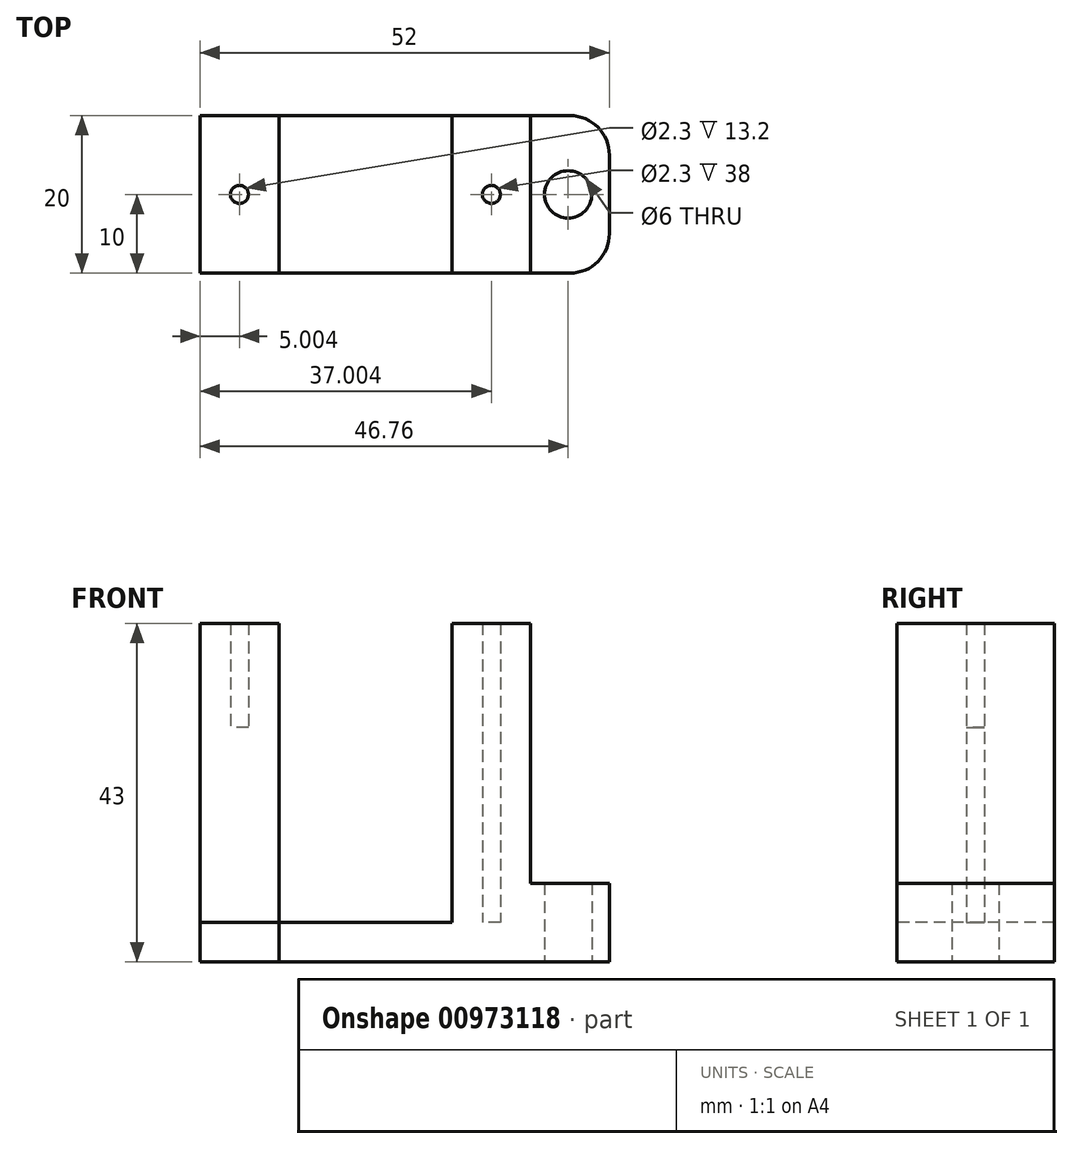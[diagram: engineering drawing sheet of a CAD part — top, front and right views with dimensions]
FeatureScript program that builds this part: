
annotation { "Feature Type Name" : "Feature", "Feature Type Description" : "" }
export const myFeature = defineFeature(function(context is Context, id is Id, definition is map)
    precondition{}
    {
        {
            var Q0;
            Q0=qCreatedBy(makeId("Top.planeOp"),FACE);
            var sketch = newSketch(context, id + "F0", { "sketchPlane" : qUnion([Q0])});
            skLineSegment(sketch, "E0.bottom", {"start": v(-30.4, 24.22) * mm, "end": v(11.6, 24.22) * mm});
            skLineSegment(sketch, "E0.top", {"start": v(-30.4, 4.22) * mm, "end": v(11.6, 4.22) * mm});
            skLineSegment(sketch, "E0.left", {"start": v(-30.4, 24.22) * mm, "end": v(-30.4, 4.22) * mm});
            skLineSegment(sketch, "E0.right", {"start": v(11.6, 24.22) * mm, "end": v(11.6, 4.22) * mm});
            skLineSegment(sketch, "E1", {"start": v(-20.4, 24.22) * mm, "end": v(-20.4, 4.22) * mm});
            skLineSegment(sketch, "E2", {"start": v(1.6, 24.22) * mm, "end": v(1.6, 4.22) * mm});
            skCircle(sketch, "E3", {"center": v(-25.4, 14.22) * mm, "radius": 1.15 * mm});
            skCircle(sketch, "E4", {"center": v(6.6, 14.22) * mm, "radius": 1.15 * mm});
            skLineSegment(sketch, "E5.bottom", {"start": v(11.6, 24.22) * mm, "end": v(21.6, 24.22) * mm});
            skLineSegment(sketch, "E5.top", {"start": v(11.6, 4.22) * mm, "end": v(21.6, 4.22) * mm});
            skLineSegment(sketch, "E5.right", {"start": v(21.6, 24.22) * mm, "end": v(21.6, 4.22) * mm});
            skCircle(sketch, "E6", {"center": v(16.36, 14.22) * mm, "radius": 3 * mm});
            skSolve(sketch);
        }
        {
            var Q0;
            {var subQ0=sQuery(id+"F0.wireOp",EDGE,"E0.left");Q0=makeQuery(id+"F0.imprint","IMPRINT",FACE,{"disambiguationData":[TD([[makeQuery(id+"F0.imprint","IMPRINT",EDGE,{"derivedFrom":subQ0}),1.0]])]});}
            var Q1;
            {var subQ1=sQuery(id+"F0.wireOp",EDGE,"E0.right");Q1=makeQuery(id+"F0.imprint","IMPRINT",FACE,{"disambiguationData":[TD([[makeQuery(id+"F0.imprint","IMPRINT",EDGE,{"derivedFrom":subQ1}),-1.0]])]});}
            var Q2;
            Q2=makeQuery(id+"F0.imprint","IMPRINT",FACE,{"disambiguationData":[TD([[makeQuery(id+"F0.imprint","IMPRINT",EDGE,{"derivedFrom":sQuery(id+"F0.wireOp",EDGE,"E3")}),1.0]])]});
            var Q3;
            {var subQ0=sQuery(id+"F0.wireOp",EDGE,"E2");Q3=makeQuery(id+"F0.imprint","IMPRINT",FACE,{"disambiguationData":[TD([[makeQuery(id+"F0.imprint","IMPRINT",EDGE,{"derivedFrom":subQ0}),1.0]])]});}
            extrude(context, id + "F1", {"entities" : qUnion([Q0, Q1, Q2, Q3]), "depth" : 43 * mm, "offsetDistance" : 25 * mm});
        }
        {
            var Q0;
            {var subQ0=sQuery(id+"F0.wireOp",EDGE,"E0.left");Q0=makeQuery(id+"F0.imprint","IMPRINT",FACE,{"disambiguationData":[TD([[makeQuery(id+"F0.imprint","IMPRINT",EDGE,{"derivedFrom":subQ0}),1.0]])]});}
            var Q1;
            Q1=makeQuery(id+"F0.imprint","IMPRINT",FACE,{"disambiguationData":[TD([[makeQuery(id+"F0.imprint","IMPRINT",EDGE,{"derivedFrom":sQuery(id+"F0.wireOp",EDGE,"E3")}),1.0]])]});
            var Q2;
            {var subQ0=sQuery(id+"F0.wireOp",EDGE,"E1");Q2=makeQuery(id+"F0.imprint","IMPRINT",FACE,{"disambiguationData":[TD([[makeQuery(id+"F0.imprint","IMPRINT",EDGE,{"derivedFrom":subQ0}),1.0]])]});}
            var Q3;
            Q3=makeQuery(id+"F0.imprint","IMPRINT",FACE,{"disambiguationData":[TD([[makeQuery(id+"F0.imprint","IMPRINT",EDGE,{"derivedFrom":sQuery(id+"F0.wireOp",EDGE,"E4")}),1.0]])]});
            var Q4;
            {var subQ1=sQuery(id+"F0.wireOp",EDGE,"E0.right");Q4=makeQuery(id+"F0.imprint","IMPRINT",FACE,{"disambiguationData":[TD([[makeQuery(id+"F0.imprint","IMPRINT",EDGE,{"derivedFrom":subQ1}),-1.0]])]});}
            extrude(context, id + "F2", {"entities" : qUnion([Q0, Q1, Q2, Q3, Q4]), "depth" : 5 * mm, "offsetDistance" : 25 * mm});
        }
        {
            var Q0;
            Q0=makeQuery(id+"F0.imprint","IMPRINT",FACE,{"disambiguationData":[TD([[makeQuery(id+"F0.imprint","IMPRINT",EDGE,{"derivedFrom":sQuery(id+"F0.wireOp",EDGE,"E3")}),1.0]])]});
            var Q1;
            Q1=makeQuery(id+"F0.imprint","IMPRINT",FACE,{"disambiguationData":[TD([[makeQuery(id+"F0.imprint","IMPRINT",EDGE,{"derivedFrom":sQuery(id+"F0.wireOp",EDGE,"E4")}),1.0]])]});
            extrude(context, id + "F3", {"entities" : qUnion([Q0, Q1]), "operationType" : NewBodyOperationType.REMOVE, "depth" : 45.5 * mm, "offsetDistance" : 25 * mm, "hasSecondDirection" : true, "secondDirectionOppositeDirection" : false, "secondDirectionDepth" : 29.8 * mm});
        }
        {
            var Q0;
            Q0=makeQuery(id+"F0.imprint","IMPRINT",FACE,{"disambiguationData":[TD([[makeQuery(id+"F0.imprint","IMPRINT",EDGE,{"derivedFrom":sQuery(id+"F0.wireOp",EDGE,"E5.bottom")}),-1.0]])]});
            extrude(context, id + "F4", {"entities" : qUnion([Q0]), "operationType" : NewBodyOperationType.ADD, "depth" : 10 * mm, "offsetDistance" : 25 * mm});
        }
        {
            var Q0;
            Q0=makeQuery(id+"F4.opExtrude","SWEPT_EDGE",EDGE,{"disambiguationData":[OSD([sQuery(id+"F0.wireOp",EDGE,"E5.top"),sQuery(id+"F0.wireOp",EDGE,"E5.right")])]});
            var Q1;
            Q1=makeQuery(id+"F4.opExtrude","SWEPT_EDGE",EDGE,{"disambiguationData":[OSD([sQuery(id+"F0.wireOp",EDGE,"E5.bottom"),sQuery(id+"F0.wireOp",EDGE,"E5.right")])]});
            fillet(context, id + "F5", {"entities" : qUnion([Q0, Q1]), "radius" : 5 * mm, "tangentPropagation" : true, "allowEdgeOverflow" : false});
        }
    });
